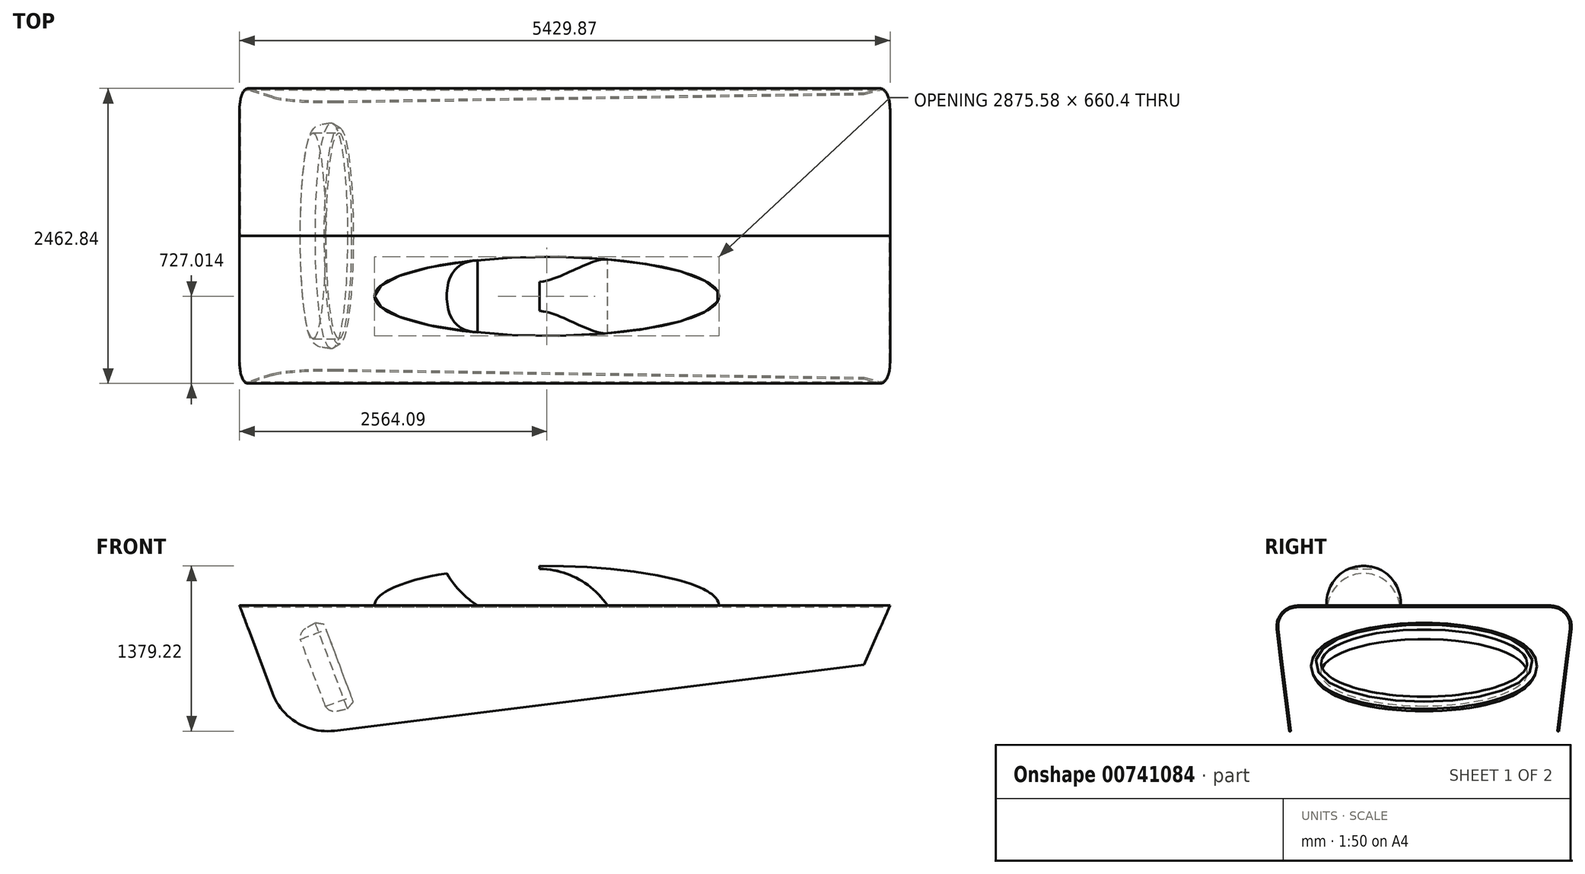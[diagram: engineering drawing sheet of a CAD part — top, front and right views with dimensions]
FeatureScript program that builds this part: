
annotation { "Feature Type Name" : "Feature", "Feature Type Description" : "" }
export const myFeature = defineFeature(function(context is Context, id is Id, definition is map)
    precondition{}
    {
        {
            var Q0;
            Q0=qCreatedBy(makeId("Front.planeOp"),FACE);
            var sketch = newSketch(context, id + "F0", { "sketchPlane" : qUnion([Q0])});
            skLineSegment(sketch, "E0", {"start": v(-7083.36, 0) * mm, "end": v(5166.33, 0) * mm, "construction": true});
            skLineSegment(sketch, "E1", {"start": v(-2505.35, 1357.06) * mm, "end": v(2924.52, 1357.06) * mm});
            skLineSegment(sketch, "E2", {"start": v(2924.52, 1357.06) * mm, "end": v(2708.45, 863.4) * mm});
            skLineSegment(sketch, "E3", {"start": v(2708.45, 863.4) * mm, "end": v(-1711.58, 311.8) * mm});
            skLineSegment(sketch, "E4", {"start": v(-2505.35, 1357.06) * mm, "end": v(-2231.24, 626.08) * mm});
            skArc(sketch, "E5", {"start": v(-2231.24, 626.08) * mm, "mid": v(-2025.94, 378.77) * mm, "end": v(-1711.58, 311.8) * mm});
            skArc(sketch, "E6", {"start": v(1496.53, 1357.06) * mm, "mid": v(781.42, 1692.4) * mm, "end": v(0, 1807.42) * mm});
            skLineSegment(sketch, "E7", {"start": v(0, 1807.42) * mm, "end": v(0, 1736.46) * mm});
            skLineSegment(sketch, "E8", {"start": v(0, 1807.42) * mm, "end": v(-333.57, 1807.42) * mm, "construction": true});
            skArc(sketch, "E9", {"start": v(572.2, 1357.06) * mm, "mid": v(343.27, 1633) * mm, "end": v(0, 1736.46) * mm});
            skLineSegment(sketch, "E10", {"start": v(0, 1736.46) * mm, "end": v(-300.37, 1736.46) * mm, "construction": true});
            skArc(sketch, "E11", {"start": v(-820.63, 1713.57) * mm, "mid": v(-1127.11, 1578.03) * mm, "end": v(-1379.05, 1357.06) * mm});
            skArc(sketch, "E12", {"start": v(-820.63, 1713.57) * mm, "mid": v(-696.06, 1513.24) * mm, "end": v(-519.27, 1357.06) * mm});
            skLineSegment(sketch, "E13", {"start": v(-2103.56, 1357.06) * mm, "end": v(-1711.58, 311.8) * mm});
            skSolve(sketch);
        }
        {
            var Q0;
            Q0=qCreatedBy(makeId("Right.planeOp"),FACE);
            var sketch = newSketch(context, id + "F1", { "sketchPlane" : qUnion([Q0])});
            skLineSegment(sketch, "E14", {"start": v(0, 1357.06) * mm, "end": v(-1056.27, 1357.06) * mm});
            skArc(sketch, "E15", {"start": v(-1056.27, 1357.06) * mm, "mid": v(-1187.39, 1298.04) * mm, "end": v(-1230.14, 1160.75) * mm});
            skLineSegment(sketch, "E16", {"start": v(-1230.14, 1160.75) * mm, "end": v(-1113.05, 198.53) * mm});
            skLineSegment(sketch, "E17.0", {"start": v(-1217.53, 1162.28) * mm, "end": v(-1100.44, 200.07) * mm});
            skArc(sketch, "E17.1", {"start": v(-1056.27, 1344.36) * mm, "mid": v(-1177.88, 1289.62) * mm, "end": v(-1217.53, 1162.28) * mm});
            skLineSegment(sketch, "E17.2", {"start": v(0, 1344.36) * mm, "end": v(-1056.27, 1344.36) * mm});
            skLineSegment(sketch, "E18", {"start": v(0, 1357.06) * mm, "end": v(0, 1344.36) * mm});
            skLineSegment(sketch, "E19", {"start": v(-1100.44, 200.07) * mm, "end": v(-1113.05, 198.53) * mm});
            skSolve(sketch);
        }
        {
            var Q0;
            Q0 = qSketchRegion(id + "F1", true);
            var Q1;
            Q1=sQuery(id+"F0.wireOp",VERTEX,"E1.start");
            var Q2;
            Q2=sQuery(id+"F0.wireOp",VERTEX,"E2.start");
            extrude(context, id + "F2", {"entities" : qUnion([Q0]), "endBound" : BoundingType.UP_TO_VERTEX, "oppositeDirection" : true, "depth" : 25.4 * mm, "endBoundEntityVertex" : qUnion([Q1]), "offsetDistance" : 25.4 * mm, "hasSecondDirection" : true, "secondDirectionBound" : SecondDirectionBoundingType.UP_TO_VERTEX, "secondDirectionOppositeDirection" : false, "secondDirectionDepth" : 25.4 * mm, "secondDirectionBoundEntityVertex" : qUnion([Q2])});
        }
        {
            var Q0;
            Q0=qCreatedBy(makeId("Front.planeOp"),FACE);
            var sketch = newSketch(context, id + "F3", { "sketchPlane" : qUnion([Q0])});
            skLineSegment(sketch, "E20.0", {"start": v(-2505.35, 1357.06) * mm, "end": v(-2231.24, 626.08) * mm});
            skArc(sketch, "E20.1", {"start": v(-2231.24, 626.08) * mm, "mid": v(-2025.94, 378.77) * mm, "end": v(-1711.58, 311.8) * mm});
            skLineSegment(sketch, "E20.2", {"start": v(2708.45, 863.4) * mm, "end": v(-1711.58, 311.8) * mm});
            skLineSegment(sketch, "E20.3", {"start": v(2924.52, 1357.06) * mm, "end": v(2708.45, 863.4) * mm});
            skLineSegment(sketch, "E21", {"start": v(-2505.35, 1357.06) * mm, "end": v(-2767.53, 1357.06) * mm});
            skLineSegment(sketch, "E22", {"start": v(-2767.53, 1357.06) * mm, "end": v(-2767.53, -671.19) * mm});
            skLineSegment(sketch, "E23", {"start": v(-2767.53, -671.19) * mm, "end": v(3371.64, -671.19) * mm});
            skLineSegment(sketch, "E24", {"start": v(3371.64, -671.19) * mm, "end": v(3371.64, 1357.06) * mm});
            skLineSegment(sketch, "E25", {"start": v(3371.64, 1357.06) * mm, "end": v(2924.52, 1357.06) * mm});
            skSolve(sketch);
        }
        {
            var Q0;
            Q0=makeQuery(id+"F3.imprint","IMPRINT",FACE,{"disambiguationData":[TD([[makeQuery(id+"F3.imprint","IMPRINT",EDGE,{"derivedFrom":sQuery(id+"F3.wireOp",EDGE,"E20.0")}),-1.0]])]});
            extrude(context, id + "F4", {"entities" : qUnion([Q0]), "operationType" : NewBodyOperationType.REMOVE, "endBound" : BoundingType.THROUGH_ALL, "depth" : 25.4 * mm, "offsetDistance" : 25.4 * mm});
        }
        {
            var Q0;
            Q0=sQuery(id+"F0.wireOp",EDGE,"E13");
            cPlane(context, id + "F5", {"entities" : qUnion([Q0]), "cplaneType" : CPlaneType.LINE_ANGLE, "offset" : 25.4 * mm, "angle" : 0 * degree, "width" : 152.4 * mm, "height" : 152.4 * mm});
        }
        {
            var Q0;
            Q0=qCreatedBy(id+"F5.planeOp",FACE);
            var sketch = newSketch(context, id + "F6", { "sketchPlane" : qUnion([Q0])});
            skEllipse(sketch, "E26", {"center": v(0, 1409.49) * mm, "majorRadius": 866.62 * mm, "minorRadius": 306.56 * mm, "majorAxis": v(1, 0)});
            skSolve(sketch);
        }
        {
            var Q0;
            Q0=qCreatedBy(makeId("Front.planeOp"),FACE);
            var sketch = newSketch(context, id + "F7", { "sketchPlane" : qUnion([Q0])});
            skLineSegment(sketch, "E27", {"start": v(-1787.83, 515.13) * mm, "end": v(-1571.5, 596.26) * mm});
            skArc(sketch, "E28", {"start": v(-1787.83, 515.13) * mm, "mid": v(-1747.34, 481.18) * mm, "end": v(-1694.74, 476.11) * mm});
            skLineSegment(sketch, "E29", {"start": v(-1694.74, 476.11) * mm, "end": v(-1604.33, 494.89) * mm});
            skLineSegment(sketch, "E30", {"start": v(-1604.33, 494.89) * mm, "end": v(-1555.47, 553.5) * mm});
            skLineSegment(sketch, "E31", {"start": v(-1555.47, 553.5) * mm, "end": v(-1571.5, 596.26) * mm});
            skSolve(sketch);
        }
        {
            var Q0;
            Q0=makeQuery(id+"F7.imprint","IMPRINT",FACE,{"disambiguationData":[TD([[makeQuery(id+"F7.imprint","IMPRINT",EDGE,{"derivedFrom":sQuery(id+"F7.wireOp",EDGE,"E27")}),-1.0]])]});
            var Q1;
            Q1=sQuery(id+"F6.wireOp",EDGE,"E26");
            sweep(context, id + "F8", {"profiles" : qUnion([Q0]), "path" : qUnion([Q1])});
        }
        {
            var Q0;
            Q0=makeQuery(id+"F2.opExtrude","SWEPT_BODY",BODY,{"disambiguationData":[OSD([sQuery(id+"F1.wireOp",EDGE,"E14"),sQuery(id+"F1.wireOp",EDGE,"E15"),sQuery(id+"F1.wireOp",EDGE,"E16"),sQuery(id+"F1.wireOp",EDGE,"E17.0"),sQuery(id+"F1.wireOp",EDGE,"E17.1"),sQuery(id+"F1.wireOp",EDGE,"E17.2"),sQuery(id+"F1.wireOp",EDGE,"E18"),sQuery(id+"F1.wireOp",EDGE,"E19")])]});
            var Q1;
            Q1=qCreatedBy(makeId("Front.planeOp"),FACE);
            mirror(context, id + "F9", {"operationType" : NewBodyOperationType.ADD, "entities" : qUnion([Q0]), "mirrorPlane" : qUnion([Q1])});
        }
        {
            var Q0;
            {var subQ0=makeQuery(id+"F2.opExtrude","SWEPT_FACE",FACE,{"disambiguationData":[OSD([sQuery(id+"F1.wireOp",EDGE,"E14")])]});Q0=makeQuery(id+"F9.boolean.opBoolean","MERGE",FACE,{"derivedFrom":[subQ0,makeQuery(id+"F9.opPattern","COPY",FACE,{"derivedFrom":subQ0,"instanceName":"1"})]});}
            var sketch = newSketch(context, id + "F10", { "sketchPlane" : qUnion([Q0])});
            skEllipse(sketch, "E32", {"center": v(58.74, -504.4) * mm, "majorRadius": 1437.8 * mm, "minorRadius": 330.2 * mm, "majorAxis": v(-1, 0)});
            skLineSegment(sketch, "E33", {"start": v(-1379.05, -504.4) * mm, "end": v(-1379.05, 0) * mm, "construction": true});
            skLineSegment(sketch, "E34", {"start": v(1496.53, -504.4) * mm, "end": v(1496.53, 0) * mm, "construction": true});
            skLineSegment(sketch, "E35", {"start": v(58.74, -174.2) * mm, "end": v(58.74, -834.6) * mm, "construction": true});
            skLineSegment(sketch, "E36", {"start": v(-1379.05, -504.4) * mm, "end": v(1496.53, -504.4) * mm});
            skFitSpline(sketch, "E37.0", {"points": [v(-1353.45, -498.95) * mm, v(-1353.75, -504.4) * mm, v(-1353.45, -509.86) * mm, v(-1352.56, -515.4) * mm, v(-1351.03, -521.06) * mm, v(-1348.82, -526.93) * mm, v(-1345.87, -533) * mm, v(-1340.89, -541.38) * mm, v(-1332.59, -552.35) * mm, v(-1319.14, -566.08) * mm, v(-1302.17, -580.15) * mm, v(-1281.71, -594.36) * mm, v(-1257.84, -608.57) * mm, v(-1230.63, -622.68) * mm, v(-1200.16, -636.6) * mm, v(-1166.5, -650.28) * mm, v(-1129.72, -663.64) * mm, v(-1089.89, -676.66) * mm, v(-1054.2, -687.18) * mm, v(-1024.2, -695.39) * mm, v(-1000.97, -701.43) * mm, v(-981.01, -706.36) * mm, v(-964.7, -710.25) * mm, v(-952.27, -713.14) * mm, v(-939.7, -716) * mm, v(-922.74, -719.75) * mm, v(-901.19, -724.34) * mm, v(-874.79, -729.7) * mm, v(-838.88, -736.62) * mm, v(-792.72, -744.88) * mm, v(-735.4, -754.13) * mm, v(-676.28, -762.71) * mm, v(-615.47, -770.6) * mm, v(-553.1, -777.81) * mm, v(-489.3, -784.3) * mm, v(-424.16, -790.08) * mm, v(-357.83, -795.12) * mm, v(-290.41, -799.41) * mm, v(-222.04, -802.96) * mm, v(-164.36, -805.27) * mm, v(-117.85, -806.73) * mm, v(-82.8, -807.63) * mm, v(-47.61, -808.33) * mm, v(-18.17, -808.75) * mm, v(5.44, -808.99) * mm, v(23.18, -809.11) * mm, v(37.99, -809.18) * mm, v(49.84, -809.2) * mm, v(58.74, -809.2) * mm, v(67.64, -809.2) * mm, v(79.5, -809.18) * mm, v(94.3, -809.11) * mm, v(112.04, -808.99) * mm, v(135.66, -808.75) * mm, v(165.1, -808.33) * mm, v(200.3, -807.63) * mm, v(235.34, -806.73) * mm, v(281.84, -805.27) * mm, v(339.52, -802.96) * mm, v(407.9, -799.41) * mm, v(475.31, -795.12) * mm, v(541.64, -790.08) * mm, v(606.77, -784.3) * mm, v(670.58, -777.81) * mm, v(732.95, -770.6) * mm, v(793.76, -762.71) * mm, v(852.89, -754.13) * mm, v(910.2, -744.88) * mm, v(956.37, -736.62) * mm, v(992.27, -729.7) * mm, v(1018.67, -724.34) * mm, v(1040.22, -719.75) * mm, v(1057.17, -716) * mm, v(1069.75, -713.14) * mm, v(1082.18, -710.25) * mm, v(1098.5, -706.36) * mm, v(1118.45, -701.43) * mm, v(1141.68, -695.39) * mm, v(1171.7, -687.18) * mm, v(1207.37, -676.66) * mm, v(1247.2, -663.64) * mm, v(1283.98, -650.28) * mm, v(1317.64, -636.6) * mm, v(1348.11, -622.68) * mm, v(1375.32, -608.57) * mm, v(1399.2, -594.36) * mm, v(1419.65, -580.15) * mm, v(1436.62, -566.08) * mm, v(1450.07, -552.35) * mm, v(1458.37, -541.38) * mm, v(1463.36, -533) * mm, v(1466.3, -526.93) * mm, v(1468.52, -521.06) * mm, v(1470.04, -515.4) * mm, v(1470.94, -509.86) * mm, v(1471.23, -504.4) * mm, v(1470.94, -498.95) * mm, v(1470.04, -493.42) * mm, v(1468.52, -487.75) * mm, v(1466.3, -481.89) * mm, v(1463.36, -475.81) * mm, v(1458.37, -467.43) * mm, v(1450.07, -456.46) * mm, v(1436.62, -442.73) * mm, v(1419.65, -428.66) * mm, v(1399.2, -414.45) * mm, v(1375.32, -400.24) * mm, v(1348.11, -386.13) * mm, v(1317.64, -372.2) * mm, v(1283.98, -358.53) * mm, v(1247.2, -345.17) * mm, v(1207.37, -332.15) * mm, v(1171.7, -321.63) * mm, v(1141.68, -313.43) * mm, v(1118.45, -307.38) * mm, v(1098.5, -302.45) * mm, v(1082.18, -298.56) * mm, v(1069.75, -295.67) * mm, v(1057.17, -292.82) * mm, v(1040.22, -289.06) * mm, v(1018.67, -284.47) * mm, v(992.27, -279.12) * mm, v(956.37, -272.19) * mm, v(910.2, -263.93) * mm, v(852.89, -254.68) * mm, v(793.76, -246.1) * mm, v(732.95, -238.2) * mm, v(670.58, -231) * mm, v(606.77, -224.5) * mm, v(541.64, -218.73) * mm, v(475.31, -213.7) * mm, v(407.9, -209.4) * mm, v(339.52, -205.85) * mm, v(281.84, -203.54) * mm, v(235.34, -202.08) * mm, v(200.3, -201.18) * mm, v(165.1, -200.48) * mm, v(135.66, -200.06) * mm, v(112.04, -199.82) * mm, v(94.3, -199.7) * mm, v(79.5, -199.64) * mm, v(67.64, -199.6) * mm, v(58.74, -199.6) * mm, v(49.84, -199.6) * mm, v(37.99, -199.64) * mm, v(23.18, -199.7) * mm, v(5.44, -199.82) * mm, v(-18.17, -200.06) * mm, v(-47.61, -200.48) * mm, v(-82.8, -201.18) * mm, v(-117.85, -202.08) * mm, v(-164.36, -203.54) * mm, v(-222.04, -205.85) * mm, v(-290.41, -209.4) * mm, v(-357.83, -213.7) * mm, v(-424.16, -218.73) * mm, v(-489.3, -224.5) * mm, v(-553.1, -231) * mm, v(-615.47, -238.2) * mm, v(-676.28, -246.1) * mm, v(-735.4, -254.68) * mm, v(-792.72, -263.93) * mm, v(-838.88, -272.19) * mm, v(-874.79, -279.12) * mm, v(-901.19, -284.47) * mm, v(-922.74, -289.06) * mm, v(-939.7, -292.82) * mm, v(-952.27, -295.67) * mm, v(-964.7, -298.56) * mm, v(-981.01, -302.45) * mm, v(-1000.97, -307.38) * mm, v(-1024.2, -313.43) * mm, v(-1054.2, -321.63) * mm, v(-1089.89, -332.15) * mm, v(-1129.72, -345.17) * mm, v(-1166.5, -358.53) * mm, v(-1200.16, -372.2) * mm, v(-1230.63, -386.13) * mm, v(-1257.84, -400.24) * mm, v(-1281.71, -414.45) * mm, v(-1302.17, -428.66) * mm, v(-1319.14, -442.73) * mm, v(-1332.59, -456.46) * mm, v(-1340.89, -467.43) * mm, v(-1345.87, -475.81) * mm, v(-1348.82, -481.89) * mm, v(-1351.03, -487.75) * mm, v(-1352.56, -493.42) * mm, v(-1353.45, -498.95) * mm, v(-1353.75, -504.4) * mm, v(-1353.45, -509.86) * mm, v(-1353.45, -498.95) * mm]});
            skSolve(sketch);
        }
        {
            var Q0;
            {var subQ0=sQuery(id+"F10.wireOp",EDGE,"E36");Q0=makeQuery(id+"F10.imprint","IMPRINT",FACE,{"disambiguationData":[TD([[makeQuery(id+"F10.imprint","IMPRINT",EDGE,{"derivedFrom":subQ0}),1.0]])]});}
            var Q1;
            Q1=sQuery(id+"F10.wireOp",EDGE,"E36");
            revolve(context, id + "F11", {"surfaceOperationType" : NewSurfaceOperationType.NEW, "entities" : qUnion([Q0]), "axis" : qUnion([Q1]), "revolveType" : RevolveType.ONE_DIRECTION, "angle" : 180 * degree});
        }
        {
            var Q0;
            Q0=qCreatedBy(makeId("Front.planeOp"),FACE);
            var sketch = newSketch(context, id + "F12", { "sketchPlane" : qUnion([Q0])});
            skArc(sketch, "E38", {"start": v(568.68, 1353.53) * mm, "mid": v(322.63, 1578.78) * mm, "end": v(0, 1663.58) * mm});
            skLineSegment(sketch, "E39", {"start": v(0, 1663.58) * mm, "end": v(0, 1703.49) * mm});
            skLineSegment(sketch, "E40.0.0", {"start": v(566.31, 1357.06) * mm, "end": v(-519.27, 1357.06) * mm});
            skArc(sketch, "E41", {"start": v(-816.16, 1703.49) * mm, "mid": v(-692.49, 1509.04) * mm, "end": v(-519.27, 1357.06) * mm});
            skPoint(sketch, "E42.0.start.orphan", {"position": v(-820.63, 1713.57) * mm});
            skLineSegment(sketch, "E43", {"start": v(-816.16, 1703.49) * mm, "end": v(0, 1703.49) * mm});
            skPoint(sketch, "E44.orphan", {"position": v(1496.53, 1357.06) * mm});
            skPoint(sketch, "E45.orphan", {"position": v(-1379.05, 1357.06) * mm});
            skLineSegment(sketch, "E46", {"start": v(0, 1663.58) * mm, "end": v(-188.27, 1666.38) * mm, "construction": true});
            skSolve(sketch);
        }
        {
            var Q0;
            Q0 = qSketchRegion(id + "F12", true);
            extrude(context, id + "F13", {"entities" : qUnion([Q0]), "operationType" : NewBodyOperationType.REMOVE, "endBound" : BoundingType.THROUGH_ALL, "depth" : 25.4 * mm, "offsetDistance" : 25.4 * mm});
        }
        {
            var Q0;
            {var subQ0=sQuery(id+"F10.wireOp",EDGE,"E37.0");var subQ1=sQuery(id+"F10.wireOp",EDGE,"E36");var subQ2=makeQuery(id+"F10.imprint","INTERSECT",VERTEX,{"disambiguationData":[OD(0.0)],"derivedFrom":[subQ1,subQ0]});Q0=makeQuery(id+"F10.imprint","IMPRINT",FACE,{"disambiguationData":[TD([[makeQuery(id+"F10.imprint","IMPRINT",EDGE,{"disambiguationData":[TD([[subQ2,-1.0]])],"derivedFrom":subQ1}),-1.0]])]});}
            var Q1;
            {var subQ0=sQuery(id+"F10.wireOp",EDGE,"E37.0");var subQ1=sQuery(id+"F10.wireOp",EDGE,"E36");var subQ2=makeQuery(id+"F10.imprint","INTERSECT",VERTEX,{"disambiguationData":[OD(0.0)],"derivedFrom":[subQ1,subQ0]});Q1=makeQuery(id+"F10.imprint","IMPRINT",FACE,{"disambiguationData":[TD([[makeQuery(id+"F10.imprint","IMPRINT",EDGE,{"disambiguationData":[TD([[subQ2,-1.0]])],"derivedFrom":subQ1}),1.0]])]});}
            extrude(context, id + "F14", {"entities" : qUnion([Q0, Q1]), "operationType" : NewBodyOperationType.REMOVE, "oppositeDirection" : true, "depth" : 25.4 * mm, "offsetDistance" : 25.4 * mm});
        }
    });
